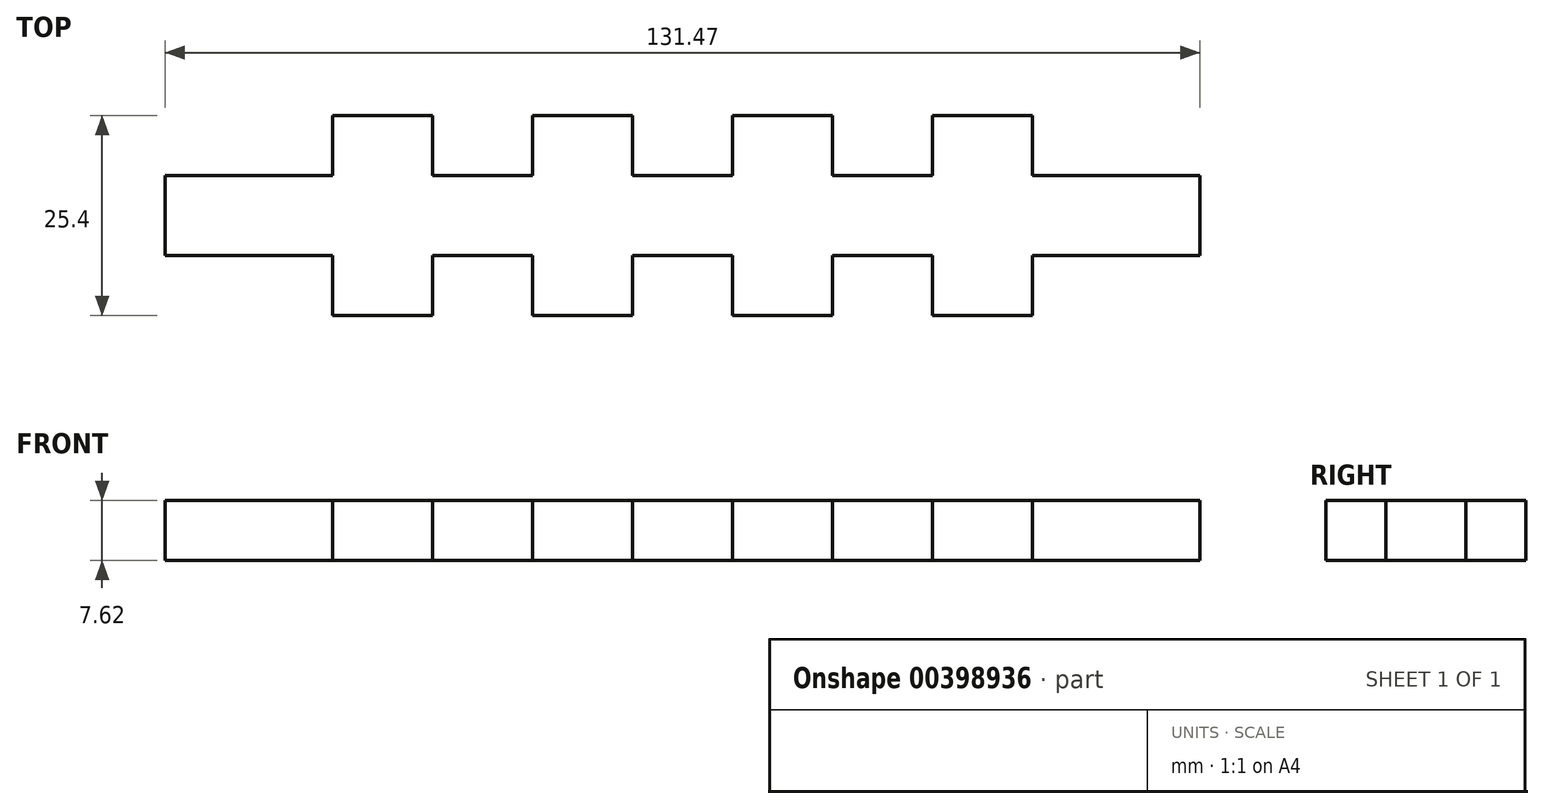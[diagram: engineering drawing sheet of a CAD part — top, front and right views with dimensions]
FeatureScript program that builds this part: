
annotation { "Feature Type Name" : "Feature", "Feature Type Description" : "" }
export const myFeature = defineFeature(function(context is Context, id is Id, definition is map)
    precondition{}
    {
        {
            var Q0;
            Q0=qCreatedBy(makeId("Top.planeOp"),FACE);
            var sketch = newSketch(context, id + "F0", { "sketchPlane" : qUnion([Q0])});
            skLineSegment(sketch, "E0.top", {"start": v(21.29, -25.4) * mm, "end": v(33.99, -25.4) * mm});
            skLineSegment(sketch, "E1", {"start": v(0, -17.78) * mm, "end": v(21.29, -17.78) * mm});
            skLineSegment(sketch, "E2", {"start": v(21.29, -17.78) * mm, "end": v(21.29, -25.4) * mm});
            skLineSegment(sketch, "E3", {"start": v(33.99, -25.4) * mm, "end": v(33.99, -17.78) * mm});
            skLineSegment(sketch, "E4", {"start": v(33.99, -17.78) * mm, "end": v(46.69, -17.78) * mm});
            skLineSegment(sketch, "E5", {"start": v(46.69, -17.78) * mm, "end": v(46.69, -25.4) * mm});
            skLineSegment(sketch, "E6", {"start": v(46.69, -25.4) * mm, "end": v(59.39, -25.4) * mm});
            skLineSegment(sketch, "E7", {"start": v(59.39, -25.4) * mm, "end": v(59.39, -17.78) * mm});
            skLineSegment(sketch, "E8", {"start": v(59.39, -17.78) * mm, "end": v(72.09, -17.78) * mm});
            skLineSegment(sketch, "E9", {"start": v(72.09, -17.78) * mm, "end": v(72.09, -25.4) * mm});
            skLineSegment(sketch, "E10", {"start": v(72.09, -25.4) * mm, "end": v(84.79, -25.4) * mm});
            skLineSegment(sketch, "E11", {"start": v(84.79, -25.4) * mm, "end": v(84.79, -17.78) * mm});
            skLineSegment(sketch, "E12", {"start": v(84.79, -17.78) * mm, "end": v(97.49, -17.78) * mm});
            skLineSegment(sketch, "E13", {"start": v(97.49, -17.78) * mm, "end": v(97.49, -25.4) * mm});
            skLineSegment(sketch, "E14.trimOffspring", {"start": v(97.49, -25.4) * mm, "end": v(110.19, -25.4) * mm});
            skLineSegment(sketch, "E15", {"start": v(110.19, -25.4) * mm, "end": v(110.19, -17.78) * mm});
            skLineSegment(sketch, "E16", {"start": v(110.19, -17.78) * mm, "end": v(131.47, -17.78) * mm});
            skPoint(sketch, "E17.orphan", {"position": v(-0.07, -25.4) * mm});
            skPoint(sketch, "E18.orphan", {"position": v(0, 0) * mm});
            skPoint(sketch, "E19.orphan", {"position": v(131.47, 0) * mm});
            skLineSegment(sketch, "E20", {"start": v(0, -17.78) * mm, "end": v(0, -7.62) * mm});
            skLineSegment(sketch, "E21", {"start": v(0, -7.62) * mm, "end": v(21.29, -7.62) * mm});
            skLineSegment(sketch, "E22", {"start": v(21.29, -7.62) * mm, "end": v(21.29, 0) * mm});
            skLineSegment(sketch, "E23", {"start": v(21.29, 0) * mm, "end": v(33.99, 0) * mm});
            skLineSegment(sketch, "E24", {"start": v(33.99, 0) * mm, "end": v(33.99, -7.62) * mm});
            skLineSegment(sketch, "E25", {"start": v(33.99, -7.62) * mm, "end": v(46.69, -7.62) * mm});
            skLineSegment(sketch, "E26", {"start": v(46.69, -7.62) * mm, "end": v(46.69, 0) * mm});
            skLineSegment(sketch, "E27", {"start": v(46.69, 0) * mm, "end": v(59.39, 0) * mm});
            skLineSegment(sketch, "E28", {"start": v(59.39, 0) * mm, "end": v(59.39, -7.62) * mm});
            skLineSegment(sketch, "E29", {"start": v(59.39, -7.62) * mm, "end": v(72.09, -7.62) * mm});
            skLineSegment(sketch, "E30", {"start": v(72.09, -7.62) * mm, "end": v(72.09, 0) * mm});
            skLineSegment(sketch, "E31", {"start": v(72.09, 0) * mm, "end": v(84.79, 0) * mm});
            skLineSegment(sketch, "E32", {"start": v(84.79, 0) * mm, "end": v(84.79, -7.62) * mm});
            skLineSegment(sketch, "E33", {"start": v(84.79, -7.62) * mm, "end": v(97.49, -7.62) * mm});
            skLineSegment(sketch, "E34", {"start": v(97.49, -7.62) * mm, "end": v(97.49, 0) * mm});
            skLineSegment(sketch, "E35", {"start": v(97.49, 0) * mm, "end": v(110.19, 0) * mm});
            skLineSegment(sketch, "E36", {"start": v(110.19, 0) * mm, "end": v(110.19, -7.62) * mm});
            skLineSegment(sketch, "E37", {"start": v(110.19, -7.62) * mm, "end": v(131.47, -7.62) * mm});
            skLineSegment(sketch, "E38", {"start": v(131.47, -7.62) * mm, "end": v(131.47, -17.78) * mm});
            skSolve(sketch);
        }
        {
            var Q0;
            Q0=makeQuery(id+"F0.imprint","IMPRINT",FACE,{"disambiguationData":[TD([[makeQuery(id+"F0.imprint","IMPRINT",EDGE,{"derivedFrom":sQuery(id+"F0.wireOp",EDGE,"E0.bottom")}),-1.0]])]});
            var Q1;
            Q1=makeQuery(id+"F0.imprint","IMPRINT",FACE,{"disambiguationData":[TD([[makeQuery(id+"F0.imprint","IMPRINT",EDGE,{"derivedFrom":sQuery(id+"F0.wireOp",EDGE,"E1")}),1.0]])]});
            extrude(context, id + "F1", {"entities" : qUnion([Q0, Q1]), "depth" : 7.62 * mm, "offsetDistance" : 25.4 * mm});
        }
    });
